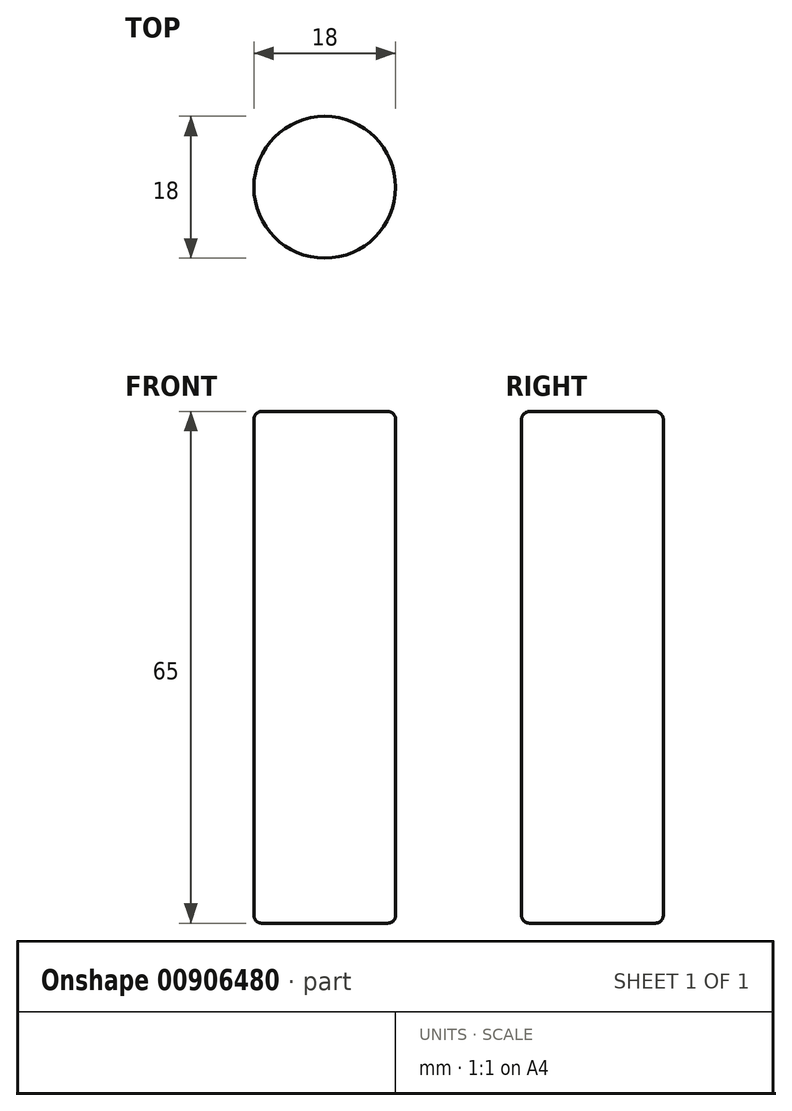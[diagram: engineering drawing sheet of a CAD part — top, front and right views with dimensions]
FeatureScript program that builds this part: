
annotation { "Feature Type Name" : "Feature", "Feature Type Description" : "" }
export const myFeature = defineFeature(function(context is Context, id is Id, definition is map)
    precondition{}
    {
        {
            var Q0;
            Q0=qCreatedBy(makeId("Front.planeOp"),FACE);
            var sketch = newSketch(context, id + "F0", { "sketchPlane" : qUnion([Q0])});
            skLineSegment(sketch, "E0.bottom", {"start": v(0, 0) * mm, "end": v(9, 0) * mm});
            skLineSegment(sketch, "E0.top", {"start": v(0, 65) * mm, "end": v(9, 65) * mm});
            skLineSegment(sketch, "E0.left", {"start": v(0, 0) * mm, "end": v(0, 65) * mm});
            skLineSegment(sketch, "E0.right", {"start": v(9, 0) * mm, "end": v(9, 65) * mm});
            skSolve(sketch);
        }
        {
            var Q0;
            Q0=makeQuery(id+"F0.imprint","IMPRINT",FACE,{"disambiguationData":[TD([[makeQuery(id+"F0.imprint","IMPRINT",EDGE,{"derivedFrom":sQuery(id+"F0.wireOp",EDGE,"E0.bottom")}),1.0]])]});
            var Q1;
            Q1=sQuery(id+"F0.wireOp",EDGE,"E0.top");
            var Q2;
            Q2=sQuery(id+"F0.wireOp",EDGE,"E0.right");
            var Q3;
            Q3=sQuery(id+"F0.wireOp",EDGE,"E0.bottom");
            var Q4;
            Q4=sQuery(id+"F0.wireOp",EDGE,"E0.left");
            revolve(context, id + "F1", {"bodyType" : ToolBodyType.SURFACE, "surfaceOperationType" : NewSurfaceOperationType.NEW, "entities" : qUnion([Q0]), "surfaceEntities" : qUnion([Q1, Q2, Q3]), "axis" : qUnion([Q4]), "revolveType" : RevolveType.FULL});
        }
        {
            var Q0;
            Q0=makeQuery(id+"F1.opRevolve","SWEPT_FACE",FACE,{"disambiguationData":[OSD([sQuery(id+"F0.wireOp",EDGE,"E0.top")])]});
            var Q1;
            Q1=makeQuery(id+"F1.opRevolve","SWEPT_FACE",FACE,{"disambiguationData":[OSD([sQuery(id+"F0.wireOp",EDGE,"E0.bottom")])]});
            fillet(context, id + "F2", {"entities" : qUnion([Q0, Q1]), "radius" : 1 * mm, "tangentPropagation" : true, "allowEdgeOverflow" : false});
        }
    });
